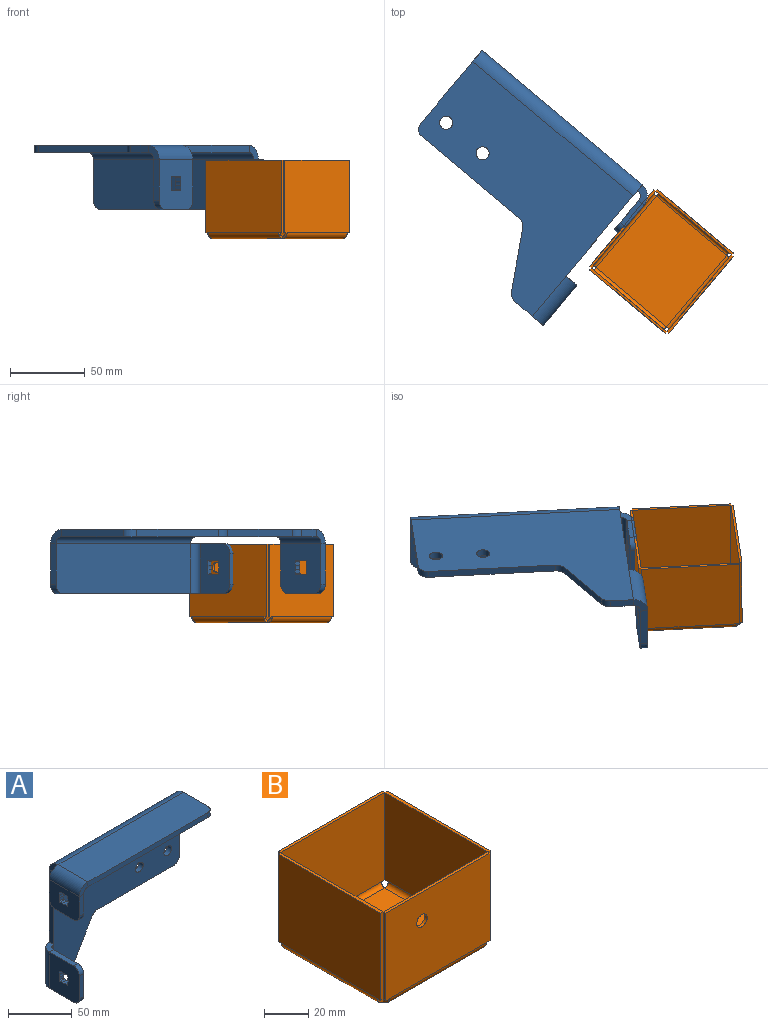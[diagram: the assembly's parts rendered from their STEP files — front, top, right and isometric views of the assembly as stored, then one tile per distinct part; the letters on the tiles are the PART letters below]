
ASSEMBLY  parts=2 mates=1
PART A: 75 faces, bbox 149.3x42.9x114.3 mm
  f0: plane 139.7x104.76mm, normal (0,-1,0), area 9712.1mm2, adj f1,f3,f7,f12,f25,f63,f64,f65
  f1: plane 15.36x4.78mm, normal (0,0,-1), area 73.3mm2, adj f0,f2,f23,f67
  f2: plane 139.7x104.76mm, normal (0,1,0), area 9712.1mm2, adj f1,f3,f7,f8,f24,f63,f64,f65
  f3: plane 53.95x4.78mm, normal (1,0,0), area 257.6mm2, adj f0,f2,f4,f66
  f4: plane 9.55x9.55mm, normal (1,0,0), area 53.7mm2, adj f3,f5,f8,f12
  f5: plane 26.98x4.78mm, normal (1,0,0), area 128.8mm2, adj f4,f9,f11,f68
  f6: plane 9.55x9.55mm, normal (-1,0,0), area 53.7mm2, adj f7,f8,f12,f14
  f7: plane 69.84x4.78mm, normal (-1,0,0), area 333.5mm2, adj f0,f2,f6,f22
  f8: cylinder r=9.55mm len=139.7mm, axis (-1,0,0), area 2095.7mm2, adj f2,f4,f6,f9
  f9: plane 139.7x33.33mm, normal (0,0,1), area 4646.8mm2, adj f5,f8,f10,f15,f68
  f10: plane 133.35x4.78mm, normal (0,-1,0), area 636.8mm2, adj f9,f11,f13,f68
  f11: plane 139.7x33.33mm, normal (0,0,-1), area 4646.8mm2, adj f5,f10,f12,f16,f68
  f12: cylinder r=4.78mm len=139.7mm, axis (-1,0,0), area 1047.9mm2, adj f0,f4,f6,f11
  f13: plane 9.55x9.55mm, normal (0,-1,0), area 53.7mm2, adj f10,f15,f16,f18
  f14: plane 9.55x9.55mm, normal (0,1,0), area 53.7mm2, adj f6,f15,f16,f17
  f15: cylinder r=9.55mm len=33.33mm, axis (0,1,0), area 499.9mm2, adj f9,f13,f14,f19
  f16: cylinder r=4.78mm len=33.33mm, axis (0,1,0), area 250mm2, adj f11,f13,f14,f20
  f17: plane 19.02x4.78mm, normal (0,1,0), area 90.8mm2, adj f14,f19,f20,f71
  f18: plane 19.02x4.78mm, normal (0,-1,0), area 90.8mm2, adj f13,f19,f20,f72
  f19: plane 33.33x25.37mm, normal (-1,0,0), area 736.6mm2, adj f15,f17,f18,f21,f47,f48,f49,f50
  f20: plane 33.33x25.37mm, normal (1,0,0), area 736.6mm2, adj f16,f17,f18,f21,f47,f48,f49,f50
  f21: plane 20.63x4.78mm, normal (0,0,-1), area 98.5mm2, adj f19,f20,f71,f72
  f22: plane 9.55x9.55mm, normal (0,0,1), area 53.7mm2, adj f7,f24,f25,f27
  f23: plane 9.55x9.55mm, normal (0,0,-1), area 53.7mm2, adj f1,f24,f25,f26
  f24: cylinder r=9.55mm len=34.93mm, axis (0,0,-1), area 523.9mm2, adj f2,f22,f23,f28
  f25: cylinder r=4.78mm len=34.93mm, axis (0,0,-1), area 262mm2, adj f0,f22,f23,f29
  f26: plane 26.98x4.78mm, normal (0,0,-1), area 128.8mm2, adj f23,f28,f29,f69
  f27: plane 26.98x4.78mm, normal (0,0,1), area 128.8mm2, adj f22,f28,f29,f70
  f28: plane 34.93x33.33mm, normal (-1,0,0), area 1054.9mm2, adj f24,f26,f27,f30,f31,f32,f33,f34
  f29: plane 34.93x33.33mm, normal (1,0,0), area 1054.9mm2, adj f25,f26,f27,f30,f31,f32,f33,f34
  f30: plane 22.23x4.78mm, normal (0,-1,0), area 106.1mm2, adj f28,f29,f69,f70
  f31: cylinder r=0.79mm len=4.78mm, axis (-1,0,0), area 6mm2, adj f28,f29,f32,f46
  f32: plane 4.78x2.58mm, normal (0,-1,0), area 12.3mm2, adj f28,f29,f31,f33
  f33: cylinder r=4.96mm len=4.78mm, axis (-1,0,0), area 13.4mm2, adj f28,f29,f32,f34
  f34: plane 4.78x2.58mm, normal (0,-1,0), area 12.3mm2, adj f28,f29,f33,f35
  f35: cylinder r=0.79mm len=4.78mm, axis (-1,0,0), area 6mm2, adj f28,f29,f34,f36
  f36: plane 4.78x2.58mm, normal (0,0,-1), area 12.3mm2, adj f28,f29,f35,f37
  f37: cylinder r=4.96mm len=4.78mm, axis (-1,0,0), area 13.4mm2, adj f28,f29,f36,f38
  f38: plane 4.78x2.58mm, normal (0,0,-1), area 12.3mm2, adj f28,f29,f37,f39
  f39: cylinder r=0.79mm len=4.78mm, axis (-1,0,0), area 6mm2, adj f28,f29,f38,f40
  f40: plane 4.78x2.58mm, normal (0,1,0), area 12.3mm2, adj f28,f29,f39,f41
  f41: cylinder r=4.96mm len=4.78mm, axis (-1,0,0), area 13.4mm2, adj f28,f29,f40,f42
  f42: plane 4.78x2.58mm, normal (0,1,0), area 12.3mm2, adj f28,f29,f41,f43
  f43: cylinder r=0.79mm len=4.78mm, axis (-1,0,0), area 6mm2, adj f28,f29,f42,f44
  f44: plane 4.78x2.58mm, normal (0,0,1), area 12.3mm2, adj f28,f29,f43,f45
  f45: cylinder r=4.96mm len=4.78mm, axis (-1,0,0), area 13.4mm2, adj f28,f29,f44,f46
  f46: plane 4.78x2.58mm, normal (0,0,1), area 12.3mm2, adj f28,f29,f31,f45
  f47: cylinder r=0.79mm len=4.78mm, axis (-1,0,0), area 6mm2, adj f19,f20,f48,f62
  f48: plane 4.78x2.58mm, normal (0,-1,0), area 12.3mm2, adj f19,f20,f47,f49
  f49: cylinder r=4.96mm len=4.78mm, axis (-1,0,0), area 13.4mm2, adj f19,f20,f48,f50
  f50: plane 4.78x2.58mm, normal (0,-1,0), area 12.3mm2, adj f19,f20,f49,f51
  f51: cylinder r=0.79mm len=4.78mm, axis (-1,0,0), area 6mm2, adj f19,f20,f50,f52
  f52: plane 4.78x2.58mm, normal (0,0,-1), area 12.3mm2, adj f19,f20,f51,f53
  f53: cylinder r=4.96mm len=4.78mm, axis (-1,0,0), area 13.4mm2, adj f19,f20,f52,f54
  f54: plane 4.78x2.58mm, normal (0,0,-1), area 12.3mm2, adj f19,f20,f53,f55
  f55: cylinder r=0.79mm len=4.78mm, axis (-1,0,0), area 6mm2, adj f19,f20,f54,f56
  f56: plane 4.78x2.58mm, normal (0,1,0), area 12.3mm2, adj f19,f20,f55,f57
  f57: cylinder r=4.96mm len=4.78mm, axis (-1,0,0), area 13.4mm2, adj f19,f20,f56,f58
  f58: plane 4.78x2.58mm, normal (0,1,0), area 12.3mm2, adj f19,f20,f57,f59
  f59: cylinder r=0.79mm len=4.78mm, axis (-1,0,0), area 6mm2, adj f19,f20,f58,f60
  f60: plane 4.78x2.58mm, normal (0,0,1), area 12.3mm2, adj f19,f20,f59,f61
  f61: cylinder r=4.96mm len=4.78mm, axis (-1,0,0), area 13.4mm2, adj f19,f20,f60,f62
  f62: plane 4.78x2.58mm, normal (0,0,1), area 12.3mm2, adj f19,f20,f47,f61
  f63: plane 38.11x22mm, normal (0.87,0,-0.5), area 210.2mm2, adj f0,f2,f65,f67
  f64: plane 84.99x4.78mm, normal (0,0,-1), area 405.8mm2, adj f0,f2,f65,f66
  f65: cylinder r=6.35mm len=5.5mm, axis (0,1,0), area 31.8mm2, adj f0,f2,f63,f64
  f66: cylinder r=6.35mm len=6.35mm, axis (0,1,0), area 47.6mm2, adj f0,f2,f3,f64
  f67: cylinder r=6.35mm len=5.5mm, axis (0,1,0), area 31.8mm2, adj f0,f1,f2,f63
  f68: cylinder r=6.35mm len=6.35mm, axis (0,0,1), area 47.6mm2, adj f5,f9,f10,f11
  f69: cylinder r=6.35mm len=6.35mm, axis (1,0,0), area 47.6mm2, adj f26,f28,f29,f30
  f70: cylinder r=6.35mm len=6.35mm, axis (1,0,0), area 47.6mm2, adj f27,f28,f29,f30
  f71: cylinder r=6.35mm len=6.35mm, axis (1,0,0), area 47.6mm2, adj f17,f19,f20,f21
  f72: cylinder r=6.35mm len=6.35mm, axis (1,0,0), area 47.6mm2, adj f18,f19,f20,f21
  f73: cylinder r=4.36mm len=8.73mm, axis (0,1,0), area 131mm2, adj f0,f2
  f74: cylinder r=4.36mm len=8.73mm, axis (0,1,0), area 131mm2, adj f0,f2
PART B: 47 faces, bbox 70.2x69.2x52.4 mm
  f0: plane 2.26x1.59mm, normal (0,0,-1), area 3.6mm2, adj f2,f6,f7,f43
  f1: plane 66.94x1.59mm, normal (0,0,1), area 106.3mm2, adj f2,f5,f6,f7
  f2: plane 48.51x1.59mm, normal (-1,0,0), area 77mm2, adj f0,f1,f6,f7
  f3: plane 2.26x1.59mm, normal (0,0,-1), area 3.6mm2, adj f5,f6,f7,f44
  f4: cylinder r=3.38mm len=6.76mm, axis (0,-1,0), area 33.7mm2, adj f6,f7
  f5: plane 48.51x1.59mm, normal (1,0,0), area 77mm2, adj f1,f3,f6,f7
  f6: plane 66.94x48.51mm, normal (0,-1,0), area 3211.8mm2, adj f0,f1,f2,f3,f4,f5,f45
  f7: plane 66.94x48.51mm, normal (0,1,0), area 3211.8mm2, adj f0,f1,f2,f3,f4,f5,f46
  f8: plane 62.42x61.43mm, normal (0,0,-1), area 3834.8mm2, adj f19,f30,f41,f45
  f9: plane 62.42x61.43mm, normal (0,0,1), area 3834.8mm2, adj f20,f31,f42,f46
  f10: plane 2.26x1.59mm, normal (0,0,-1), area 3.6mm2, adj f12,f15,f16,f18
  f11: plane 66.94x1.59mm, normal (0,0,1), area 106.3mm2, adj f12,f14,f15,f16
  f12: plane 48.51x1.59mm, normal (1,0,0), area 77mm2, adj f10,f11,f15,f16
  f13: plane 2.26x1.59mm, normal (0,0,-1), area 3.6mm2, adj f14,f15,f16,f17
  f14: plane 48.51x1.59mm, normal (-1,0,0), area 77mm2, adj f11,f13,f15,f16
  f15: plane 66.94x48.51mm, normal (0,1,0), area 3247.7mm2, adj f10,f11,f12,f13,f14,f19
  f16: plane 66.94x48.51mm, normal (0,-1,0), area 3247.7mm2, adj f10,f11,f12,f13,f14,f20
  f17: plane 3.87x3.87mm, normal (-1,0,0), area 7.7mm2, adj f13,f19,f20,f39
  f18: plane 3.87x3.87mm, normal (1,0,0), area 7.7mm2, adj f10,f19,f20,f28
  f19: cylinder r=3.87mm len=62.42mm, axis (-1,0,0), area 379.8mm2, adj f8,f15,f17,f18
  f20: cylinder r=2.29mm len=62.42mm, axis (-1,0,0), area 224.1mm2, adj f9,f16,f17,f18
  f21: plane 2.26x1.59mm, normal (0,0,-1), area 3.6mm2, adj f23,f26,f27,f29
  f22: plane 65.95x1.59mm, normal (0,0,1), area 104.7mm2, adj f23,f25,f26,f27
  f23: plane 48.51x1.59mm, normal (0,-1,0), area 77mm2, adj f21,f22,f26,f27
  f24: plane 2.26x1.59mm, normal (0,0,-1), area 3.6mm2, adj f25,f26,f27,f28
  f25: plane 48.51x1.59mm, normal (0,1,0), area 77mm2, adj f22,f24,f26,f27
  f26: plane 65.95x48.51mm, normal (1,0,0), area 3199.7mm2, adj f21,f22,f23,f24,f25,f30
  f27: plane 65.95x48.51mm, normal (-1,0,0), area 3199.7mm2, adj f21,f22,f23,f24,f25,f31
  f28: plane 3.87x3.87mm, normal (0,1,0), area 7.7mm2, adj f18,f24,f30,f31
  f29: plane 3.87x3.87mm, normal (0,-1,0), area 7.7mm2, adj f21,f30,f31,f44
  f30: cylinder r=3.87mm len=61.43mm, axis (0,1,0), area 373.8mm2, adj f8,f26,f28,f29
  f31: cylinder r=2.29mm len=61.43mm, axis (0,1,0), area 220.6mm2, adj f9,f27,f28,f29
  f32: plane 2.26x1.59mm, normal (0,0,-1), area 3.6mm2, adj f34,f37,f38,f39
  f33: plane 65.95x1.59mm, normal (0,0,1), area 104.7mm2, adj f34,f36,f37,f38
  f34: plane 48.51x1.59mm, normal (0,1,0), area 77mm2, adj f32,f33,f37,f38
  f35: plane 2.26x1.59mm, normal (0,0,-1), area 3.6mm2, adj f36,f37,f38,f40
  f36: plane 48.51x1.59mm, normal (0,-1,0), area 77mm2, adj f33,f35,f37,f38
  f37: plane 65.95x48.51mm, normal (-1,0,0), area 3199.7mm2, adj f32,f33,f34,f35,f36,f41
  f38: plane 65.95x48.51mm, normal (1,0,0), area 3199.7mm2, adj f32,f33,f34,f35,f36,f42
  f39: plane 3.87x3.87mm, normal (0,1,0), area 7.7mm2, adj f17,f32,f41,f42
  f40: plane 3.87x3.87mm, normal (0,-1,0), area 7.7mm2, adj f35,f41,f42,f43
  f41: cylinder r=3.87mm len=61.43mm, axis (0,1,0), area 373.8mm2, adj f8,f37,f39,f40
  f42: cylinder r=2.29mm len=61.43mm, axis (0,1,0), area 220.6mm2, adj f9,f38,f39,f40
  f43: plane 3.87x3.87mm, normal (-1,0,0), area 7.7mm2, adj f0,f40,f45,f46
  f44: plane 3.87x3.87mm, normal (1,0,0), area 7.7mm2, adj f3,f29,f45,f46
  f45: cylinder r=3.87mm len=62.42mm, axis (-1,0,0), area 379.8mm2, adj f6,f8,f43,f44
  f46: cylinder r=2.29mm len=62.42mm, axis (-1,0,0), area 224.1mm2, adj f7,f9,f43,f44
PLACE A rot(axis=(0.25,0.68,0.68),152deg) t=(-120.58,132.19,-33.14)mm
PLACE B rot(axis=(0,0,-1),130deg) t=(-140.08,11.12,-88.96)mm
MATE fastened A.f49 <-> B.f4  axis (0.77,-0.64,0) through (-69.96,68.99,-53.76)mm
